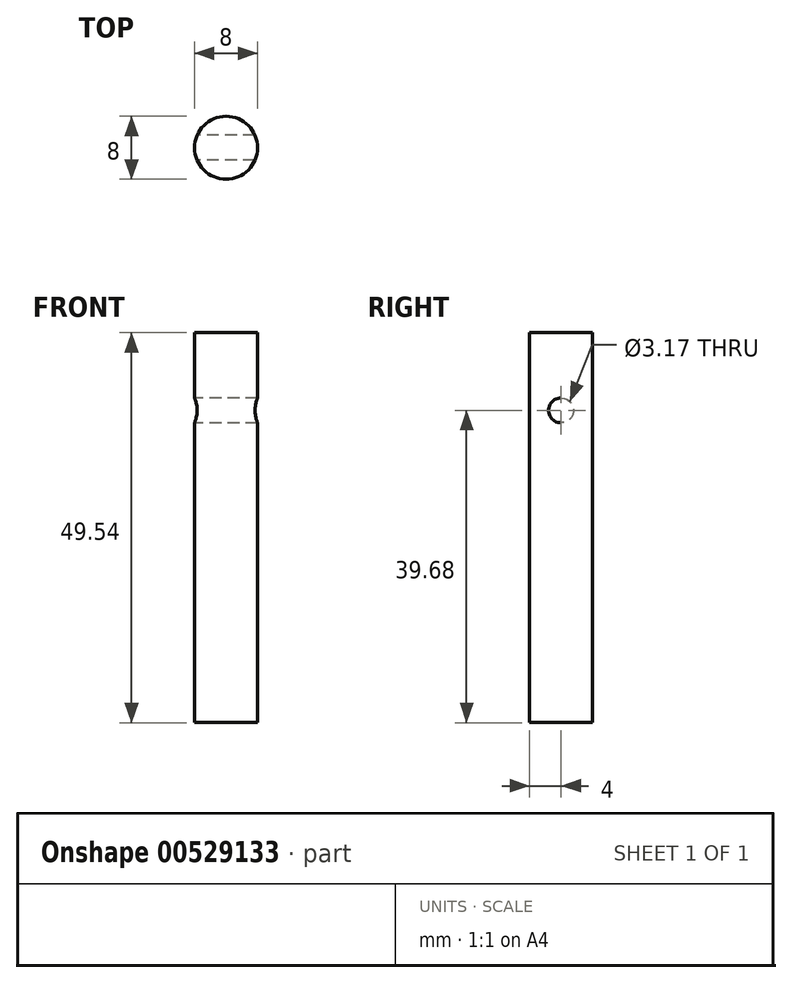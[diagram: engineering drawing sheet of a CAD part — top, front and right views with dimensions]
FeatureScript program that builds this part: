
annotation { "Feature Type Name" : "Feature", "Feature Type Description" : "" }
export const myFeature = defineFeature(function(context is Context, id is Id, definition is map)
    precondition{}
    {
        {
            var Q0;
            Q0=qCreatedBy(makeId("Right.planeOp"),FACE);
            var sketch = newSketch(context, id + "F0", { "sketchPlane" : qUnion([Q0])});
            skLineSegment(sketch, "E0.bottom", {"start": v(-4.66, 24.77) * mm, "end": v(4.66, 24.77) * mm});
            skLineSegment(sketch, "E0.top", {"start": v(-4.66, -24.77) * mm, "end": v(4.66, -24.77) * mm});
            skLineSegment(sketch, "E0.left", {"start": v(-4.66, 24.77) * mm, "end": v(-4.66, -24.77) * mm});
            skLineSegment(sketch, "E0.right", {"start": v(4.66, 24.77) * mm, "end": v(4.66, -24.77) * mm});
            skPoint(sketch, "E0.middle", {"position": v(0, 0) * mm});
            skLineSegment(sketch, "E1", {"start": v(0, 24.77) * mm, "end": v(0, -24.77) * mm, "construction": true});
            skCircle(sketch, "E2", {"center": v(0, 14.9) * mm, "radius": 1.59 * mm});
            skSolve(sketch);
        }
        {
            var Q0;
            Q0 = qSketchRegion(id + "F0", true);
            extrude(context, id + "F1", {"entities" : qUnion([Q0]), "depth" : 4.83 * mm, "offsetDistance" : 25.4 * mm, "hasSecondDirection" : true, "secondDirectionOppositeDirection" : true, "secondDirectionDepth" : 4.06 * mm});
        }
        {
            var Q0;
            Q0=makeQuery(id+"F1.opExtrude","SWEPT_FACE",FACE,{"disambiguationData":[OSD([sQuery(id+"F0.wireOp",EDGE,"E0.bottom")])]});
            var sketch = newSketch(context, id + "F2", { "sketchPlane" : qUnion([Q0])});
            skCircle(sketch, "E3", {"center": v(0, 0) * mm, "radius": 4 * mm});
            skSolve(sketch);
        }
        {
            var Q0;
            Q0=makeQuery(id+"F2.imprint","IMPRINT",FACE,{"disambiguationData":[TD([[makeQuery(id+"F2.imprint","IMPRINT",EDGE,{"derivedFrom":sQuery(id+"F2.wireOp",EDGE,"E3")}),-1.0]])]});
            extrude(context, id + "F3", {"entities" : qUnion([Q0]), "operationType" : NewBodyOperationType.REMOVE, "oppositeDirection" : true, "depth" : 49.53 * mm, "offsetDistance" : 25.4 * mm});
        }
    });
